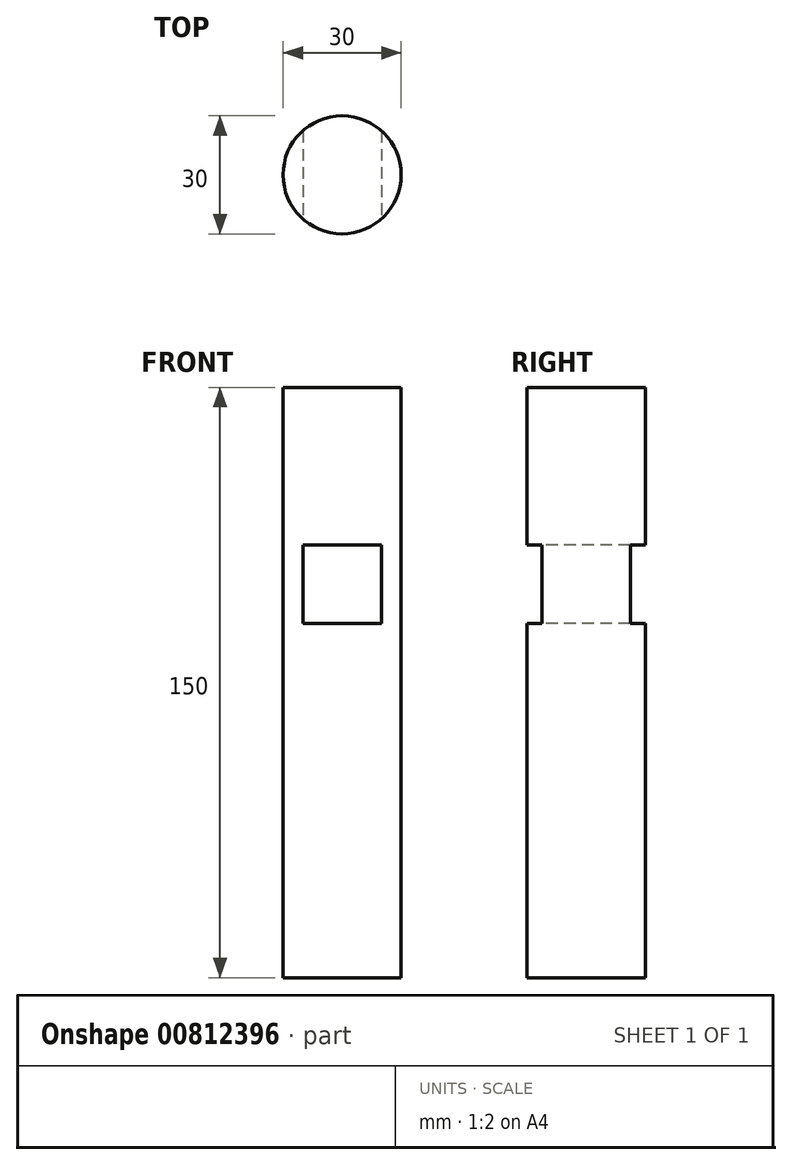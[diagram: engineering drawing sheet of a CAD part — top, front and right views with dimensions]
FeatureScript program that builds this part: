
annotation { "Feature Type Name" : "Feature", "Feature Type Description" : "" }
export const myFeature = defineFeature(function(context is Context, id is Id, definition is map)
    precondition{}
    {
        {
            var Q0;
            Q0=qCreatedBy(makeId("Top.planeOp"),FACE);
            var sketch = newSketch(context, id + "F0", { "sketchPlane" : qUnion([Q0])});
            skCircle(sketch, "E0", {"center": v(0, 0.88) * mm, "radius": 15 * mm});
            skSolve(sketch);
        }
        {
            var Q0;
            Q0=makeQuery(id+"F0.imprint","IMPRINT",FACE,{"disambiguationData":[TD([[makeQuery(id+"F0.imprint","IMPRINT",EDGE,{"derivedFrom":sQuery(id+"F0.wireOp",EDGE,"E0")}),1.0]])]});
            extrude(context, id + "F1", {"entities" : qUnion([Q0]), "depth" : 150 * mm, "offsetDistance" : 25 * mm});
        }
        {
            var Q0;
            Q0=qCreatedBy(makeId("Front.planeOp"),FACE);
            var sketch = newSketch(context, id + "F2", { "sketchPlane" : qUnion([Q0])});
            skLineSegment(sketch, "E1.bottom", {"start": v(-10, 110) * mm, "end": v(10, 110) * mm});
            skLineSegment(sketch, "E1.top", {"start": v(-10, 90) * mm, "end": v(10, 90) * mm});
            skLineSegment(sketch, "E1.left", {"start": v(-10, 110) * mm, "end": v(-10, 90) * mm});
            skLineSegment(sketch, "E1.right", {"start": v(10, 110) * mm, "end": v(10, 90) * mm});
            skLineSegment(sketch, "E2", {"start": v(0, 0) * mm, "end": v(0, 6.32) * mm});
            skSolve(sketch);
        }
        {
            var Q0;
            Q0 = qSketchRegion(id + "F2", true);
            extrude(context, id + "F3", {"entities" : qUnion([Q0]), "operationType" : NewBodyOperationType.REMOVE, "endBound" : BoundingType.SYMMETRIC, "oppositeDirection" : true, "depth" : 50 * mm, "offsetDistance" : 25 * mm});
        }
    });
